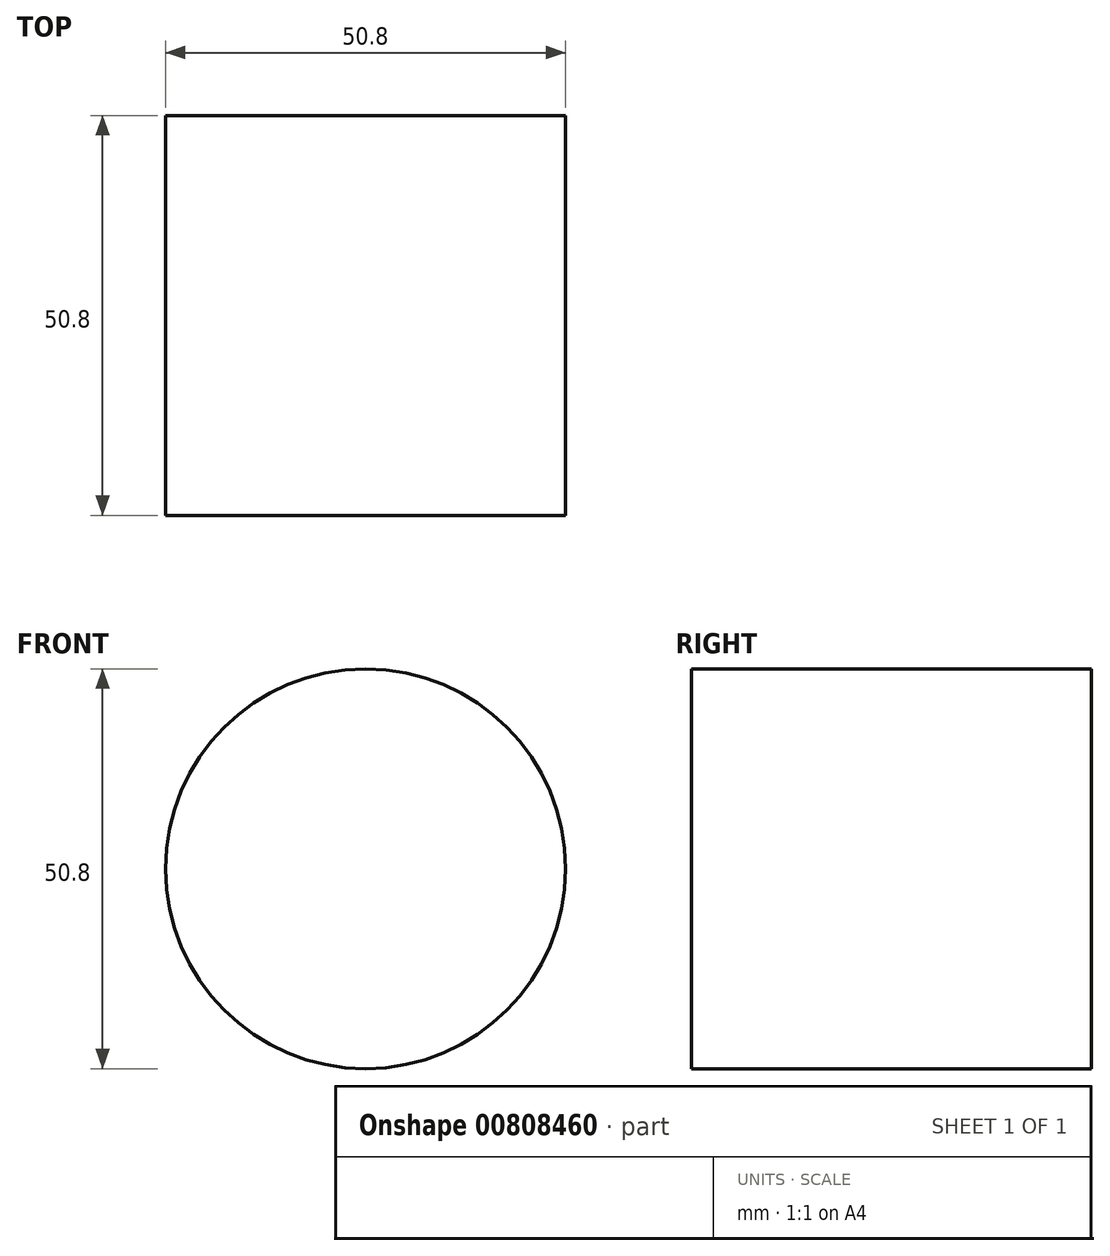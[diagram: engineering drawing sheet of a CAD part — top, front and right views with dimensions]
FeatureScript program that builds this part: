
annotation { "Feature Type Name" : "Feature", "Feature Type Description" : "" }
export const myFeature = defineFeature(function(context is Context, id is Id, definition is map)
    precondition{}
    {
        {
            var Q0;
            Q0=qCreatedBy(makeId("Front.planeOp"),FACE);
            var sketch = newSketch(context, id + "F0", { "sketchPlane" : qUnion([Q0])});
            skLineSegment(sketch, "E0", {"start": v(-29.66, 36.63) * mm, "end": v(7.09, 36.63) * mm});
            skLineSegment(sketch, "E1", {"start": v(-42.36, 52.97) * mm, "end": v(-42.36, 49.33) * mm});
            skCircle(sketch, "E2", {"center": v(46.44, 25.4) * mm, "radius": 25.4 * mm});
            skPoint(sketch, "E3.newPointA", {"position": v(-43.71, 36.63) * mm});
            skArc(sketch, "E3.filletArc", {"start": v(-42.36, 49.33) * mm, "mid": v(-38.64, 40.34) * mm, "end": v(-29.66, 36.63) * mm});
            skLineSegment(sketch, "E4", {"start": v(0, 0) * mm, "end": v(46.44, 0) * mm});
            skSolve(sketch);
        }
        {
            var Q0;
            Q0=makeQuery(id+"F0.imprint","IMPRINT",FACE,{"disambiguationData":[TD([[makeQuery(id+"F0.imprint","IMPRINT",EDGE,{"derivedFrom":sQuery(id+"F0.wireOp",EDGE,"E2")}),1.0]])]});
            extrude(context, id + "F1", {"entities" : qUnion([Q0]), "depth" : 50.8 * mm, "offsetDistance" : 25.4 * mm});
        }
    });
